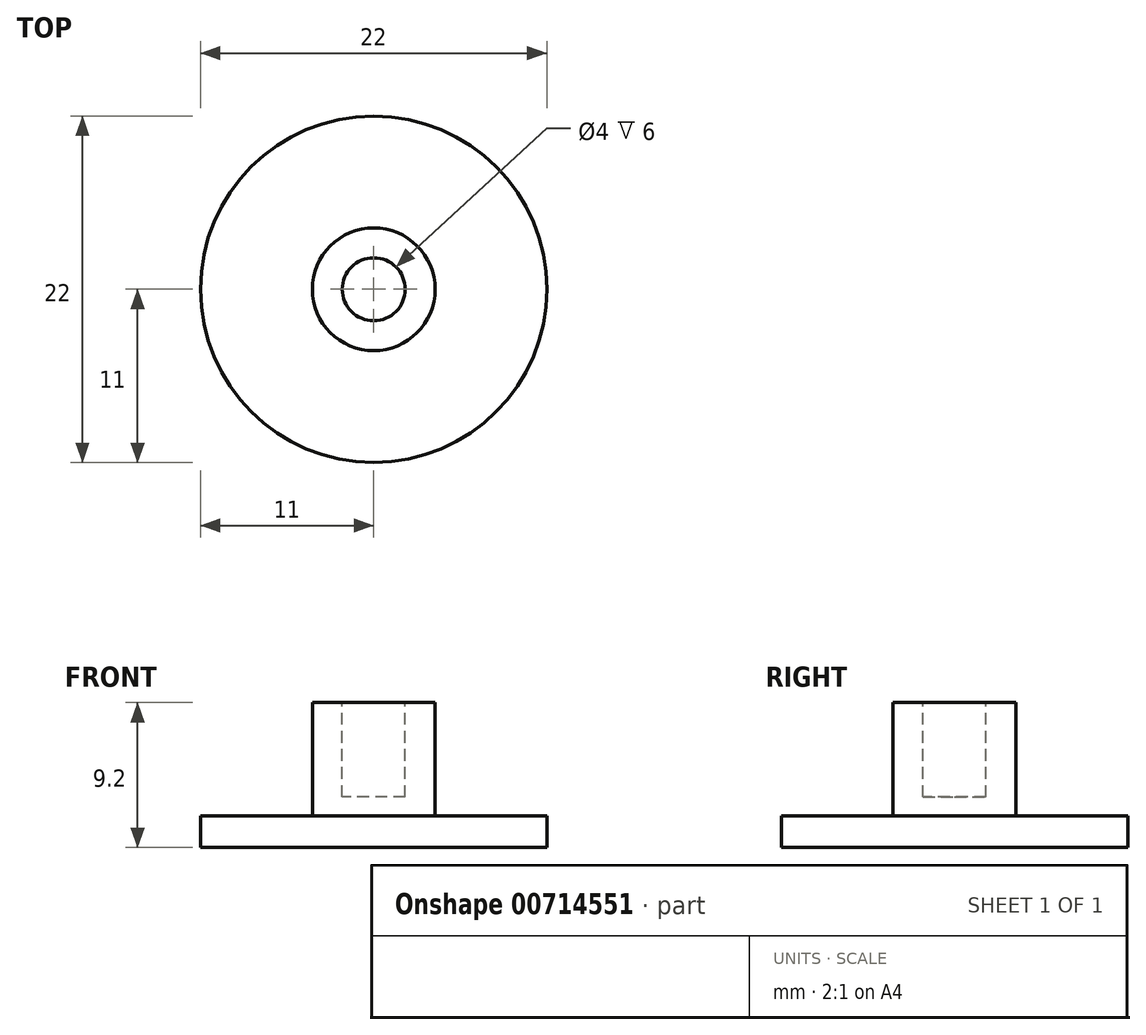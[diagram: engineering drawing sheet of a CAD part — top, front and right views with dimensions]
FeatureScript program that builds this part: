
annotation { "Feature Type Name" : "Feature", "Feature Type Description" : "" }
export const myFeature = defineFeature(function(context is Context, id is Id, definition is map)
    precondition{}
    {
        {
            var Q0;
            Q0=qCreatedBy(makeId("Top.planeOp"),FACE);
            var sketch = newSketch(context, id + "F0", { "sketchPlane" : qUnion([Q0])});
            skCircle(sketch, "E0", {"center": v(0, 0) * mm, "radius": 11 * mm});
            skSolve(sketch);
        }
        {
            var Q0;
            Q0=makeQuery(id+"F0.imprint","IMPRINT",FACE,{"disambiguationData":[TD([[makeQuery(id+"F0.imprint","IMPRINT",EDGE,{"derivedFrom":sQuery(id+"F0.wireOp",EDGE,"E0")}),1.0]])]});
            extrude(context, id + "F1", {"entities" : qUnion([Q0]), "depth" : 2 * mm, "offsetDistance" : 25 * mm});
        }
        {
            var Q0;
            Q0=makeQuery(id+"F1.opExtrude","CAP_FACE",FACE,{"disambiguationData":[OSD([sQuery(id+"F0.wireOp",EDGE,"E0")])],"isStart":false});
            var sketch = newSketch(context, id + "F2", { "sketchPlane" : qUnion([Q0])});
            skCircle(sketch, "E1", {"center": v(0, 0) * mm, "radius": 3.9 * mm});
            skSolve(sketch);
        }
        {
            var Q0;
            Q0 = qSketchRegion(id + "F2", true);
            extrude(context, id + "F3", {"entities" : qUnion([Q0]), "operationType" : NewBodyOperationType.ADD, "depth" : 7.2 * mm, "offsetDistance" : 25 * mm});
        }
        {
            var Q0;
            Q0=makeQuery(id+"F3.opExtrude","CAP_FACE",FACE,{"disambiguationData":[OSD([sQuery(id+"F2.wireOp",EDGE,"E1")])],"isStart":false});
            var sketch = newSketch(context, id + "F4", { "sketchPlane" : qUnion([Q0])});
            skCircle(sketch, "E2", {"center": v(0, 0) * mm, "radius": 2 * mm});
            skSolve(sketch);
        }
        {
            var Q0;
            Q0 = qSketchRegion(id + "F4", true);
            extrude(context, id + "F5", {"entities" : qUnion([Q0]), "operationType" : NewBodyOperationType.REMOVE, "depth" : -6 * mm, "offsetDistance" : 25 * mm});
        }
    });
